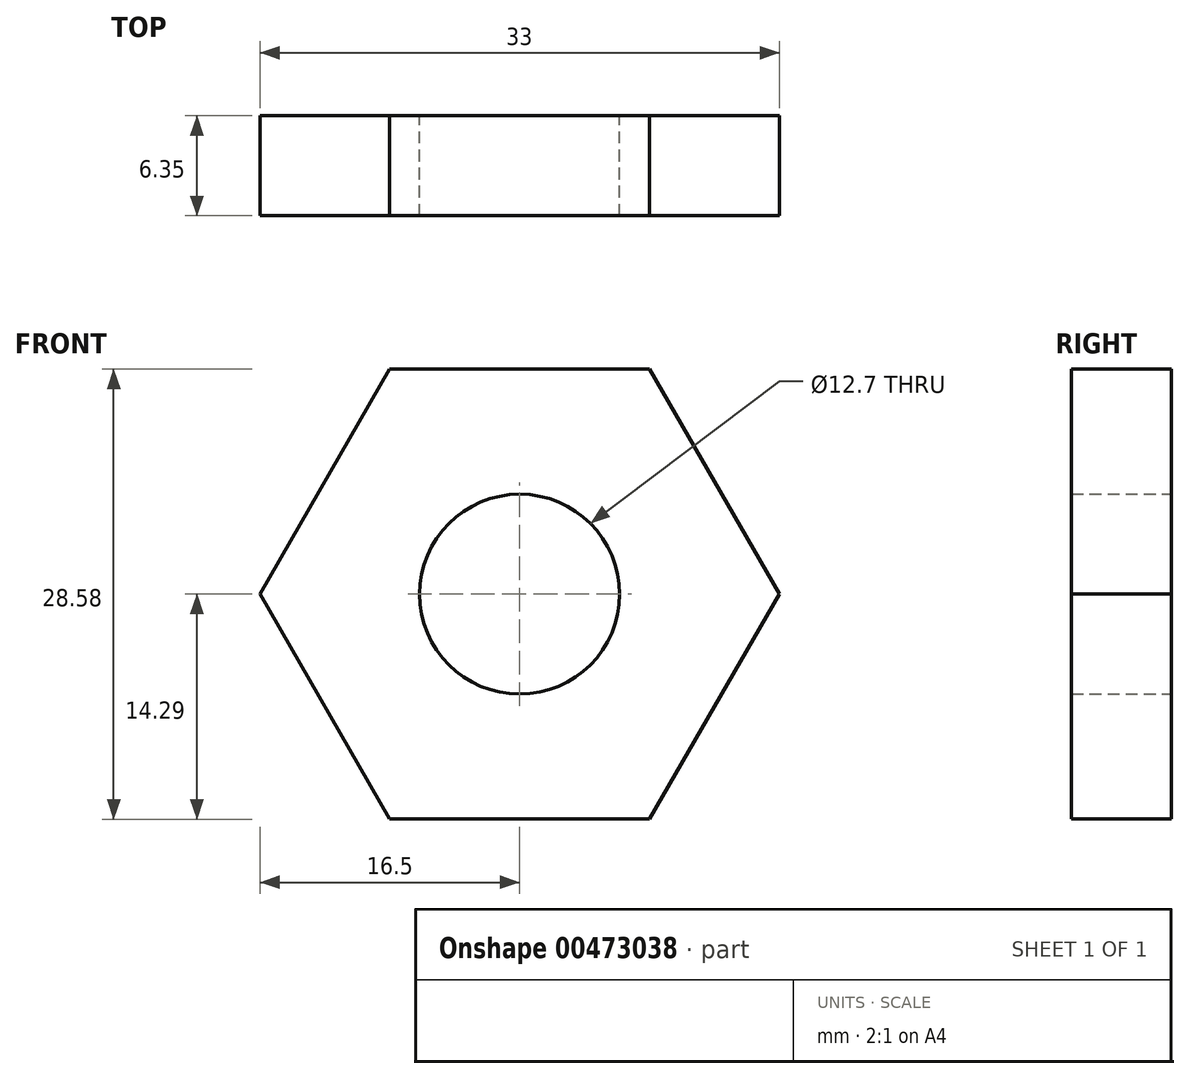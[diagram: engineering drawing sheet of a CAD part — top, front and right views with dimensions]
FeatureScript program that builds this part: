
annotation { "Feature Type Name" : "Feature", "Feature Type Description" : "" }
export const myFeature = defineFeature(function(context is Context, id is Id, definition is map)
    precondition{}
    {
        {
            var Q0;
            Q0=qCreatedBy(makeId("Front.planeOp"),FACE);
            var sketch = newSketch(context, id + "F0", { "sketchPlane" : qUnion([Q0])});
            skCircle(sketch, "E0.cCircle", {"center": v(0, 0) * mm, "radius": 14.29 * mm, "construction": true});
            skLineSegment(sketch, "E0.0", {"start": v(-8.25, 14.29) * mm, "end": v(8.25, 14.29) * mm});
            skLineSegment(sketch, "E0.1", {"start": v(8.25, 14.29) * mm, "end": v(16.5, 0) * mm});
            skLineSegment(sketch, "E0.2", {"start": v(16.5, 0) * mm, "end": v(8.25, -14.29) * mm});
            skLineSegment(sketch, "E0.3", {"start": v(8.25, -14.29) * mm, "end": v(-8.25, -14.29) * mm});
            skLineSegment(sketch, "E0.4", {"start": v(-8.25, -14.29) * mm, "end": v(-16.5, 0) * mm});
            skLineSegment(sketch, "E0.5", {"start": v(-16.5, 0) * mm, "end": v(-8.25, 14.29) * mm});
            skPoint(sketch, "E0.0.midPoint", {"position": v(0, 14.29) * mm});
            skCircle(sketch, "E1", {"center": v(0, 0) * mm, "radius": 6.35 * mm});
            skSolve(sketch);
        }
        {
            var Q0;
            Q0=makeQuery(id+"F0.imprint","IMPRINT",FACE,{"disambiguationData":[TD([[makeQuery(id+"F0.imprint","IMPRINT",EDGE,{"derivedFrom":sQuery(id+"F0.wireOp",EDGE,"E0.0")}),-1.0]])]});
            extrude(context, id + "F1", {"entities" : qUnion([Q0]), "depth" : 6.35 * mm});
        }
    });
